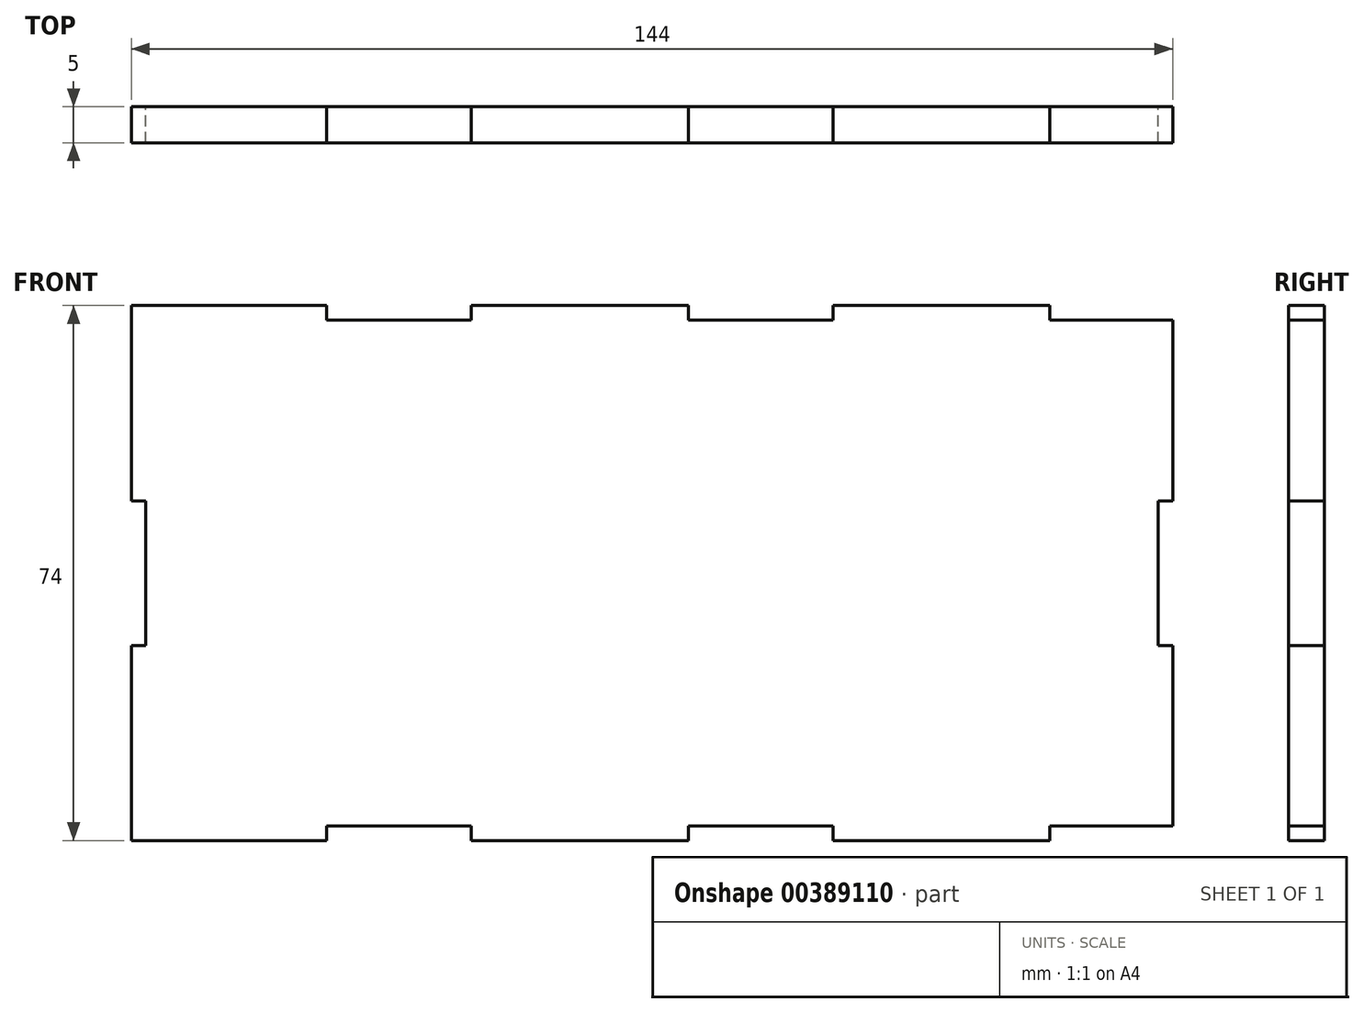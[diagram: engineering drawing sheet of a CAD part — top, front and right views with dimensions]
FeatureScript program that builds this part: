
annotation { "Feature Type Name" : "Feature", "Feature Type Description" : "" }
export const myFeature = defineFeature(function(context is Context, id is Id, definition is map)
    precondition{}
    {
        {
            var Q0;
            Q0=qCreatedBy(makeId("Front.planeOp"),FACE);
            var sketch = newSketch(context, id + "F0", { "sketchPlane" : qUnion([Q0])});
            skLineSegment(sketch, "E0", {"start": v(0, 0) * mm, "end": v(0, 27) * mm});
            skLineSegment(sketch, "E1", {"start": v(0, 27) * mm, "end": v(2, 27) * mm});
            skLineSegment(sketch, "E2", {"start": v(2, 27) * mm, "end": v(2, 47) * mm});
            skLineSegment(sketch, "E3", {"start": v(2, 47) * mm, "end": v(0, 47) * mm});
            skLineSegment(sketch, "E4", {"start": v(0, 47) * mm, "end": v(0, 74) * mm});
            skLineSegment(sketch, "E5", {"start": v(0, 74) * mm, "end": v(27, 74) * mm});
            skLineSegment(sketch, "E6", {"start": v(27, 74) * mm, "end": v(27, 72) * mm});
            skLineSegment(sketch, "E7", {"start": v(27, 72) * mm, "end": v(47, 72) * mm});
            skLineSegment(sketch, "E8", {"start": v(47, 72) * mm, "end": v(47, 74) * mm});
            skLineSegment(sketch, "E9", {"start": v(47, 74) * mm, "end": v(77, 74) * mm});
            skLineSegment(sketch, "E10", {"start": v(77, 74) * mm, "end": v(77, 72) * mm});
            skLineSegment(sketch, "E11", {"start": v(77, 72) * mm, "end": v(97, 72) * mm});
            skLineSegment(sketch, "E12", {"start": v(97, 72) * mm, "end": v(97, 74) * mm});
            skLineSegment(sketch, "E13", {"start": v(97, 74) * mm, "end": v(127, 74) * mm});
            skLineSegment(sketch, "E14", {"start": v(127, 74) * mm, "end": v(127, 72) * mm});
            skLineSegment(sketch, "E15", {"start": v(127, 72) * mm, "end": v(144, 72) * mm});
            skLineSegment(sketch, "E16", {"start": v(144, 72) * mm, "end": v(144, 47) * mm});
            skLineSegment(sketch, "E17", {"start": v(144, 47) * mm, "end": v(142, 47) * mm});
            skLineSegment(sketch, "E18", {"start": v(142, 47) * mm, "end": v(142, 27) * mm});
            skLineSegment(sketch, "E19", {"start": v(142, 27) * mm, "end": v(144, 27) * mm});
            skLineSegment(sketch, "E20", {"start": v(144, 27) * mm, "end": v(144, 2) * mm});
            skLineSegment(sketch, "E21", {"start": v(144, 2) * mm, "end": v(127, 2) * mm});
            skLineSegment(sketch, "E22", {"start": v(127, 2) * mm, "end": v(127, 0) * mm});
            skLineSegment(sketch, "E23", {"start": v(127, 0) * mm, "end": v(97, 0) * mm});
            skLineSegment(sketch, "E24", {"start": v(97, 0) * mm, "end": v(97, 2) * mm});
            skLineSegment(sketch, "E25", {"start": v(97, 2) * mm, "end": v(77, 2) * mm});
            skLineSegment(sketch, "E26", {"start": v(77, 2) * mm, "end": v(77, 0) * mm});
            skLineSegment(sketch, "E27", {"start": v(77, 0) * mm, "end": v(47, 0) * mm});
            skLineSegment(sketch, "E28", {"start": v(47, 0) * mm, "end": v(47, 2) * mm});
            skLineSegment(sketch, "E29", {"start": v(47, 2) * mm, "end": v(27, 2) * mm});
            skLineSegment(sketch, "E30", {"start": v(27, 2) * mm, "end": v(27, 0) * mm});
            skLineSegment(sketch, "E31", {"start": v(27, 0) * mm, "end": v(0, 0) * mm});
            skSolve(sketch);
        }
        {
            var Q0;
            Q0=makeQuery(id+"F0.imprint","IMPRINT",FACE,{"disambiguationData":[TD([[makeQuery(id+"F0.imprint","IMPRINT",EDGE,{"derivedFrom":sQuery(id+"F0.wireOp",EDGE,"E0")}),-1.0]])]});
            extrude(context, id + "F1", {"entities" : qUnion([Q0]), "depth" : 5 * mm});
        }
    });
